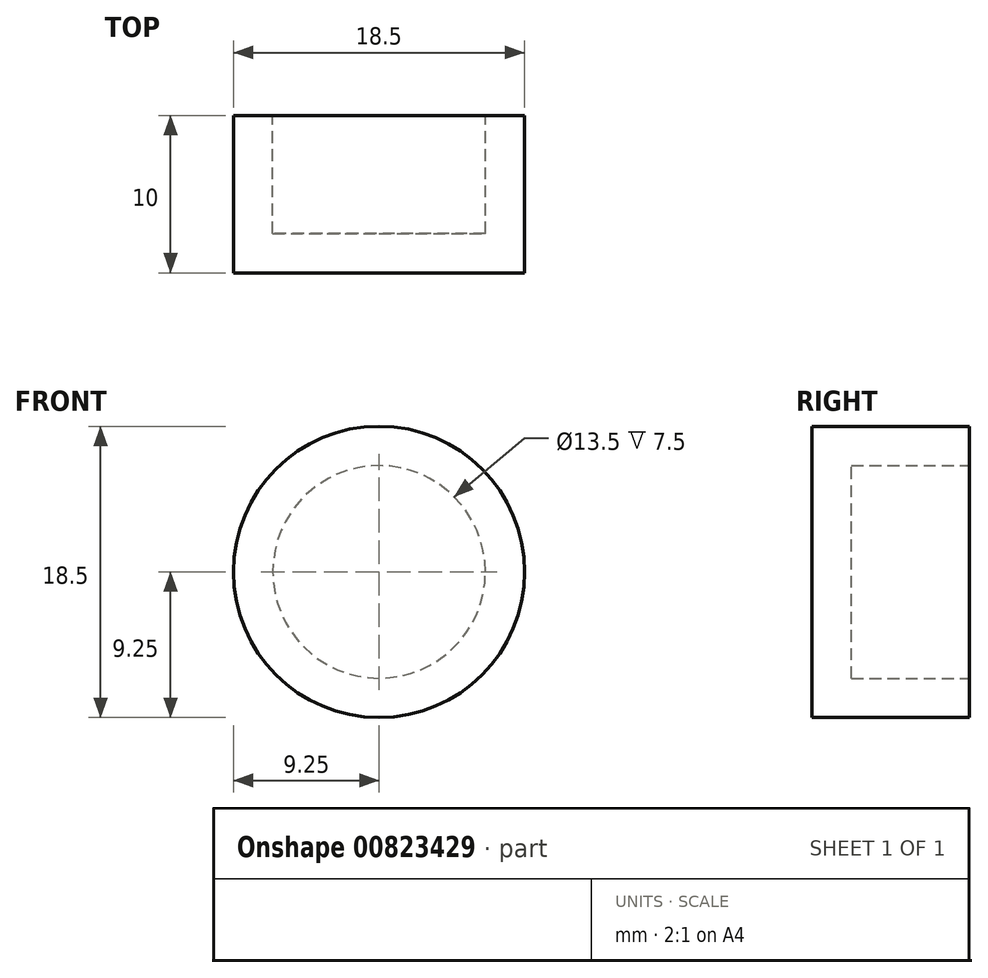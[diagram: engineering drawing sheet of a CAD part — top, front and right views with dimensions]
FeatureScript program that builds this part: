
annotation { "Feature Type Name" : "Feature", "Feature Type Description" : "" }
export const myFeature = defineFeature(function(context is Context, id is Id, definition is map)
    precondition{}
    {
        {
            var Q0;
            Q0=qCreatedBy(makeId("Front.planeOp"),FACE);
            var sketch = newSketch(context, id + "F0", { "sketchPlane" : qUnion([Q0])});
            skCircle(sketch, "E0", {"center": v(0, 0) * mm, "radius": 9.25 * mm});
            skSolve(sketch);
        }
        {
            var Q0;
            Q0=qSketchRegion(id+"F0",true);
            extrude(context, id + "F1", {"entities" : qUnion([Q0]), "depth" : 10 * mm, "offsetDistance" : 25 * mm});
        }
        {
            var Q0;
            Q0=makeQuery(id+"F1.opExtrude","CAP_FACE",FACE,{"disambiguationData":[OSD([sQuery(id+"F0.wireOp",EDGE,"E0")])],"isStart":true});
            shell(context, id + "F2", {"entities" : qUnion([Q0]), "thickness" : 2.5 * mm});
        }
    });
